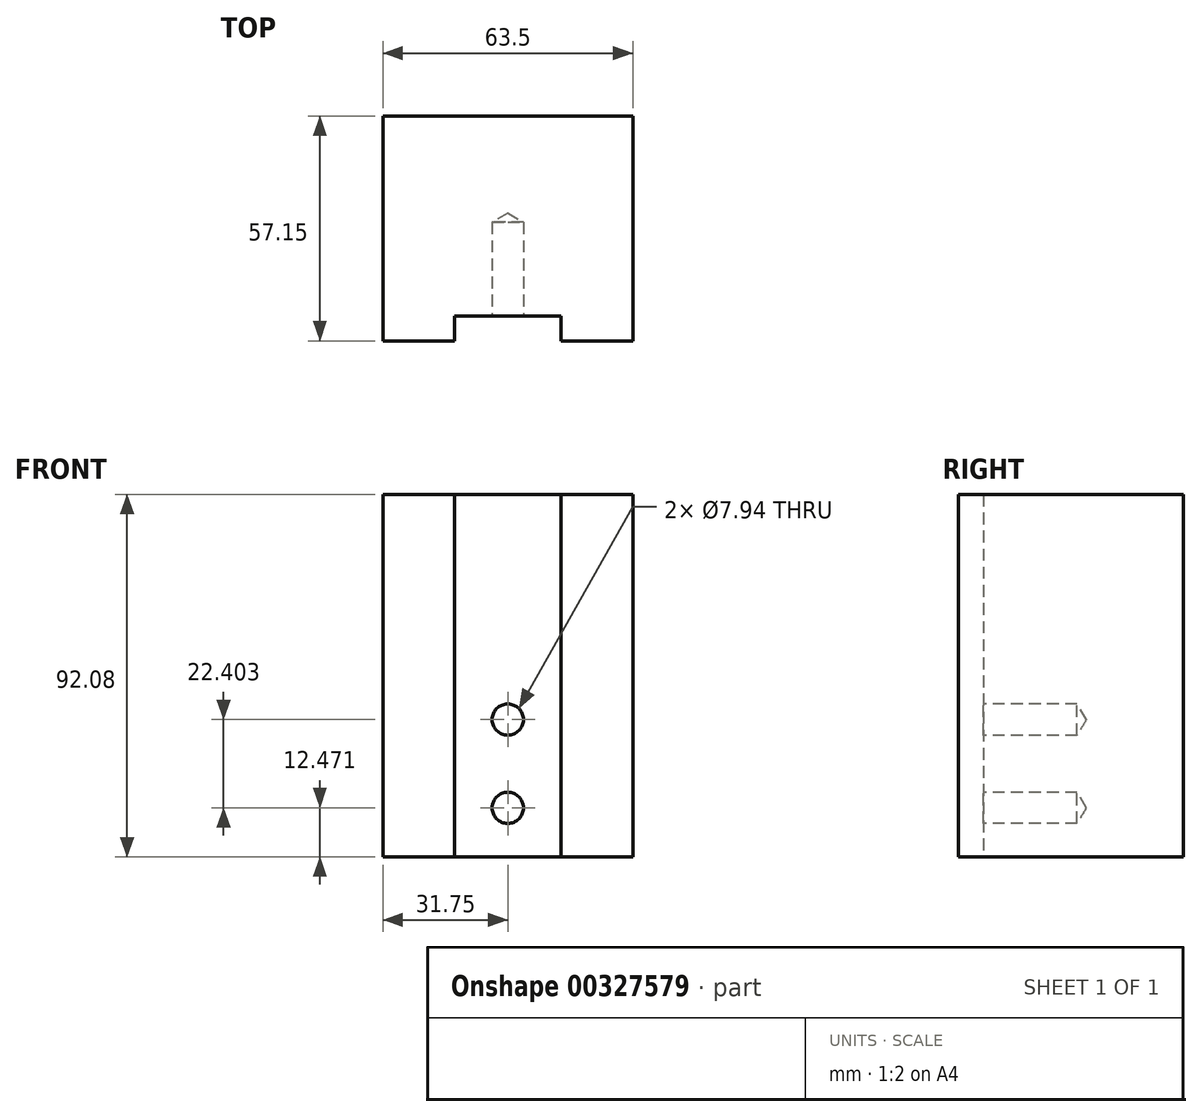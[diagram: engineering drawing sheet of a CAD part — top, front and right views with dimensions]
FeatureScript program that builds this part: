
annotation { "Feature Type Name" : "Feature", "Feature Type Description" : "" }
export const myFeature = defineFeature(function(context is Context, id is Id, definition is map)
    precondition{}
    {
        {
            var Q0;
            Q0=qCreatedBy(makeId("Top.planeOp"),FACE);
            var sketch = newSketch(context, id + "F0", { "sketchPlane" : qUnion([Q0])});
            skLineSegment(sketch, "E0", {"start": v(-31.75, 0) * mm, "end": v(-31.75, 57.15) * mm});
            skLineSegment(sketch, "E1", {"start": v(-31.75, 57.15) * mm, "end": v(31.75, 57.15) * mm});
            skLineSegment(sketch, "E2", {"start": v(31.75, 57.15) * mm, "end": v(31.75, 0) * mm});
            skLineSegment(sketch, "E3", {"start": v(31.75, 0) * mm, "end": v(13.53, 0) * mm});
            skLineSegment(sketch, "E4", {"start": v(13.53, 0) * mm, "end": v(13.53, 6.35) * mm});
            skLineSegment(sketch, "E5", {"start": v(13.53, 6.35) * mm, "end": v(-13.53, 6.35) * mm});
            skLineSegment(sketch, "E6", {"start": v(-13.53, 6.35) * mm, "end": v(-13.53, 0) * mm});
            skLineSegment(sketch, "E7", {"start": v(-13.53, 0) * mm, "end": v(-31.75, 0) * mm});
            skSolve(sketch);
        }
        {
            var Q0;
            Q0=makeQuery(id+"F0.imprint","IMPRINT",FACE,{"disambiguationData":[TD([[makeQuery(id+"F0.imprint","IMPRINT",EDGE,{"derivedFrom":sQuery(id+"F0.wireOp",EDGE,"E0")}),-1.0]])]});
            extrude(context, id + "F1", {"entities" : qUnion([Q0]), "depth" : 92.07 * mm});
        }
        {
            var Q0;
            Q0=makeQuery(id+"F1.opExtrude","SWEPT_FACE",FACE,{"disambiguationData":[OSD([sQuery(id+"F0.wireOp",EDGE,"E5")])]});
            var sketch = newSketch(context, id + "F2", { "sketchPlane" : qUnion([Q0])});
            skCircle(sketch, "E8", {"center": v(0, 12.47) * mm, "radius": 3.97 * mm});
            skCircle(sketch, "E9", {"center": v(0, 34.87) * mm, "radius": 3.97 * mm});
            skSolve(sketch);
        }
        {
            var Q0;
            Q0=sQuery(id+"F2.wireOp",VERTEX,"E9.center");
            var Q1;
            Q1=sQuery(id+"F2.wireOp",VERTEX,"E8.center");
            var Q2;
            Q2=makeQuery(id+"F1.opExtrude","SWEPT_BODY",BODY,{"disambiguationData":[OSD([sQuery(id+"F0.wireOp",EDGE,"E0"),sQuery(id+"F0.wireOp",EDGE,"E1"),sQuery(id+"F0.wireOp",EDGE,"E2"),sQuery(id+"F0.wireOp",EDGE,"E3"),sQuery(id+"F0.wireOp",EDGE,"E4"),sQuery(id+"F0.wireOp",EDGE,"E5"),sQuery(id+"F0.wireOp",EDGE,"E6"),sQuery(id+"F0.wireOp",EDGE,"E7")])]});
            hole(context, id + "F3", {"style" : HoleStyle.SIMPLE, "endStyle" : HoleEndStyle.BLIND, "standardTappedOrClearance" : lookupTablePath({ "standard" : "ANSI", "engagement" : "75%", "pitch" : "16 tpi", "size" : "3/8", "type" : "Tapped" }), "standardBlindInLast" : lookupTablePath({ "standard" : "ANSI", "engagement" : "75%", "pitch" : "16 tpi", "size" : "3/8", "type" : "Tapped" }), "holeDiameter" : 7.94 * mm, "showTappedDepth" : true, "holeDepth" : 23.8 * mm, "tappedDepth" : 19.04 * mm, "tapClearance" : 3, "locations" : qUnion([Q0, Q1]), "scope" : qUnion([Q2]), "majorDiameter" : 9.53 * mm});
        }
    });
